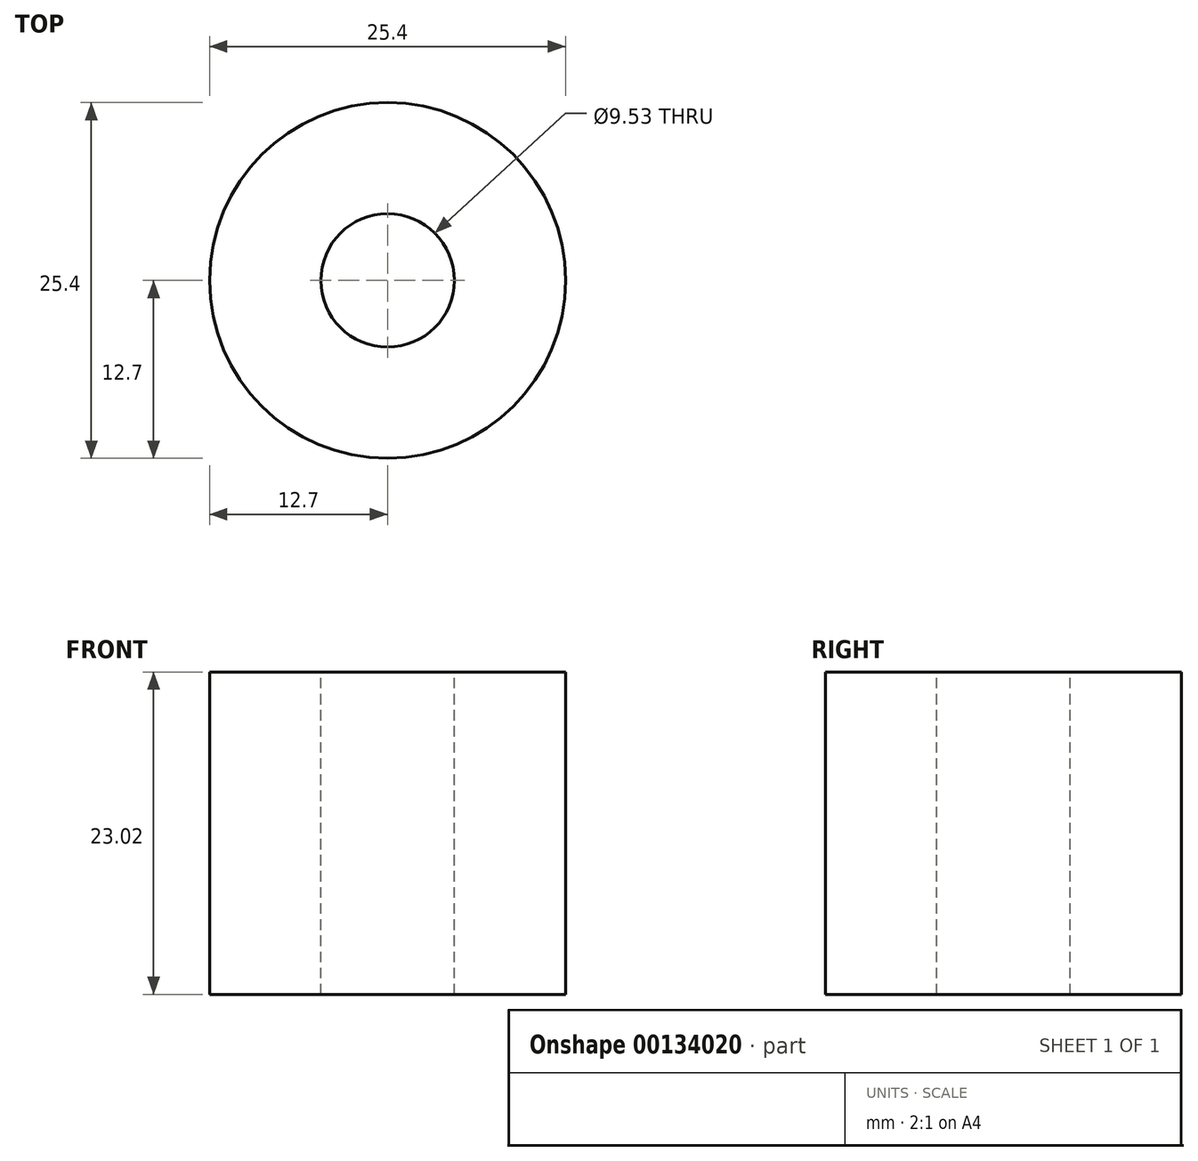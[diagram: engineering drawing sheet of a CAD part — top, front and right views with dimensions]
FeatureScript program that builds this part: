
annotation { "Feature Type Name" : "Feature", "Feature Type Description" : "" }
export const myFeature = defineFeature(function(context is Context, id is Id, definition is map)
    precondition{}
    {
        {
            var Q0;
            Q0=qCreatedBy(makeId("Top.planeOp"),FACE);
            var sketch = newSketch(context, id + "F0", { "sketchPlane" : qUnion([Q0])});
            skCircle(sketch, "E0", {"center": v(0, 0) * mm, "radius": 12.7 * mm});
            skSolve(sketch);
        }
        {
            var Q0;
            Q0 = qSketchRegion(id + "F0", true);
            extrude(context, id + "F1", {"entities" : qUnion([Q0]), "endBound" : BoundingType.SYMMETRIC, "depth" : 23.02 * mm});
        }
        {
            var Q0;
            Q0=makeQuery(id+"F1.opExtrude","CAP_FACE",FACE,{"disambiguationData":[OSD([sQuery(id+"F0.wireOp",EDGE,"E0")])],"isStart":false});
            var sketch = newSketch(context, id + "F2", { "sketchPlane" : qUnion([Q0])});
            skPoint(sketch, "E1", {"position": v(0, 0) * mm});
            skSolve(sketch);
        }
        {
            var Q0;
            Q0=sQuery(id+"F2.wireOp",VERTEX,"E1");
            var Q1;
            Q1=makeQuery(id+"F1.opExtrude","SWEPT_BODY",BODY,{"disambiguationData":[OSD([sQuery(id+"F0.wireOp",EDGE,"E0")])]});
            hole(context, id + "F3", {"style" : HoleStyle.SIMPLE, "endStyle" : HoleEndStyle.THROUGH, "holeDiameter" : 9.52 * mm, "locations" : qUnion([Q0]), "scope" : qUnion([Q1]), "isTappedThrough" : true});
        }
    });
